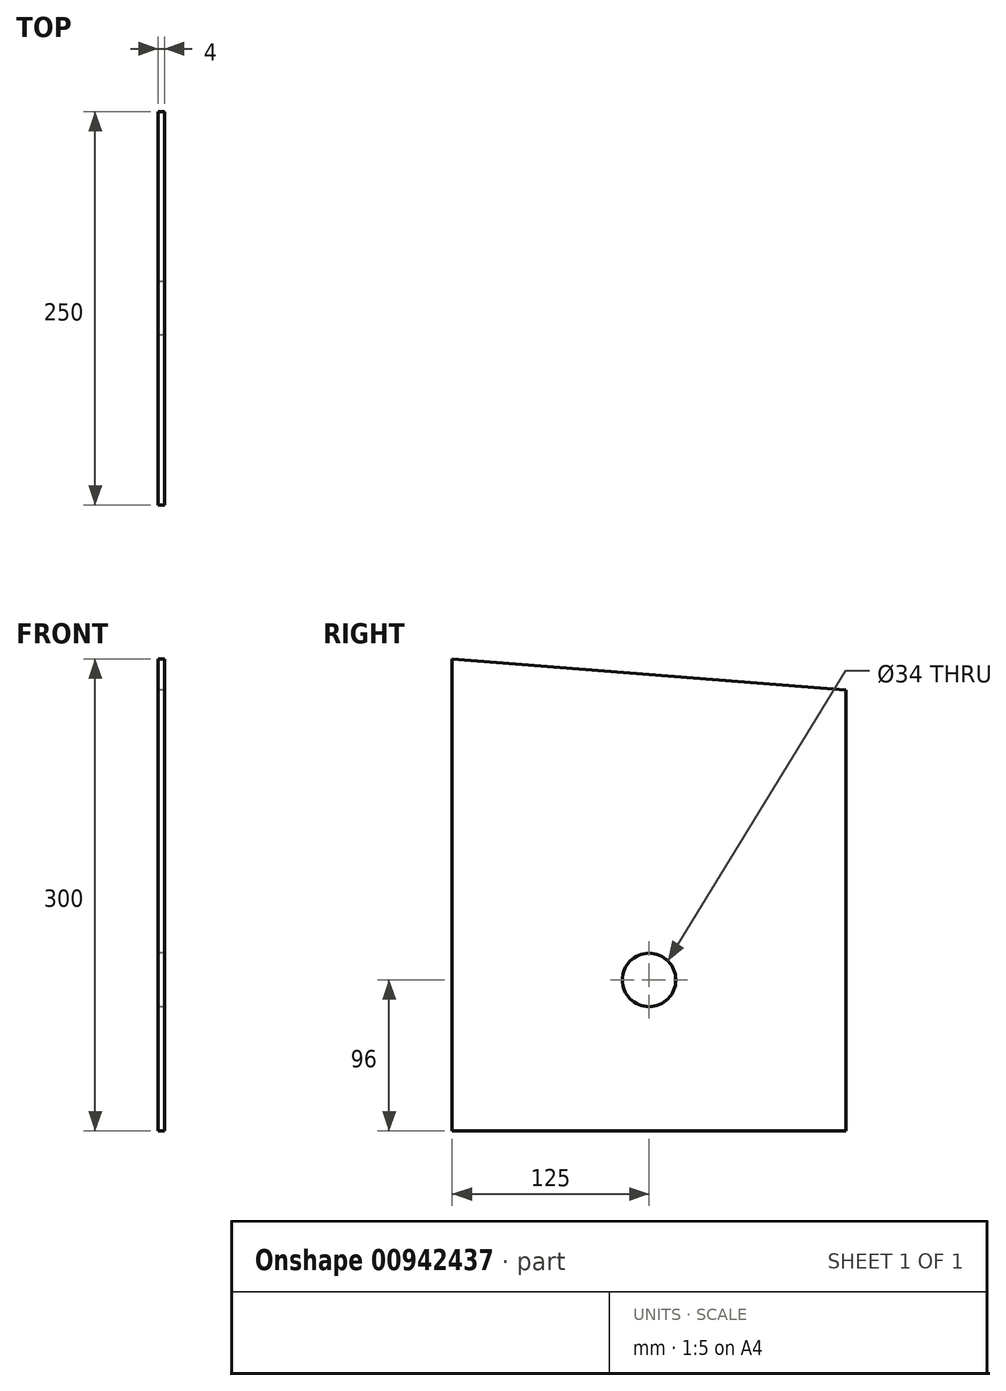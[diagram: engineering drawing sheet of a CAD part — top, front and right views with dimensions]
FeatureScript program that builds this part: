
annotation { "Feature Type Name" : "Feature", "Feature Type Description" : "" }
export const myFeature = defineFeature(function(context is Context, id is Id, definition is map)
    precondition{}
    {
        {
            var Q0;
            Q0=qCreatedBy(makeId("Right.planeOp"),FACE);
            var sketch = newSketch(context, id + "F0", { "sketchPlane" : qUnion([Q0])});
            skLineSegment(sketch, "E0.bottom", {"start": v(-125, 0) * mm, "end": v(125, 0) * mm});
            skLineSegment(sketch, "E0.left", {"start": v(-125, 0) * mm, "end": v(-125, 300) * mm});
            skLineSegment(sketch, "E0.right", {"start": v(125, 0) * mm, "end": v(125, 280) * mm});
            skLineSegment(sketch, "E1", {"start": v(-125, 300) * mm, "end": v(125, 280) * mm});
            skCircle(sketch, "E2", {"center": v(0, 96) * mm, "radius": 17 * mm});
            skSolve(sketch);
        }
        {
            var Q0;
            Q0 = qSketchRegion(id + "F0", true);
            extrude(context, id + "F1", {"entities" : qUnion([Q0]), "depth" : 4 * mm, "offsetDistance" : 25 * mm});
        }
    });
